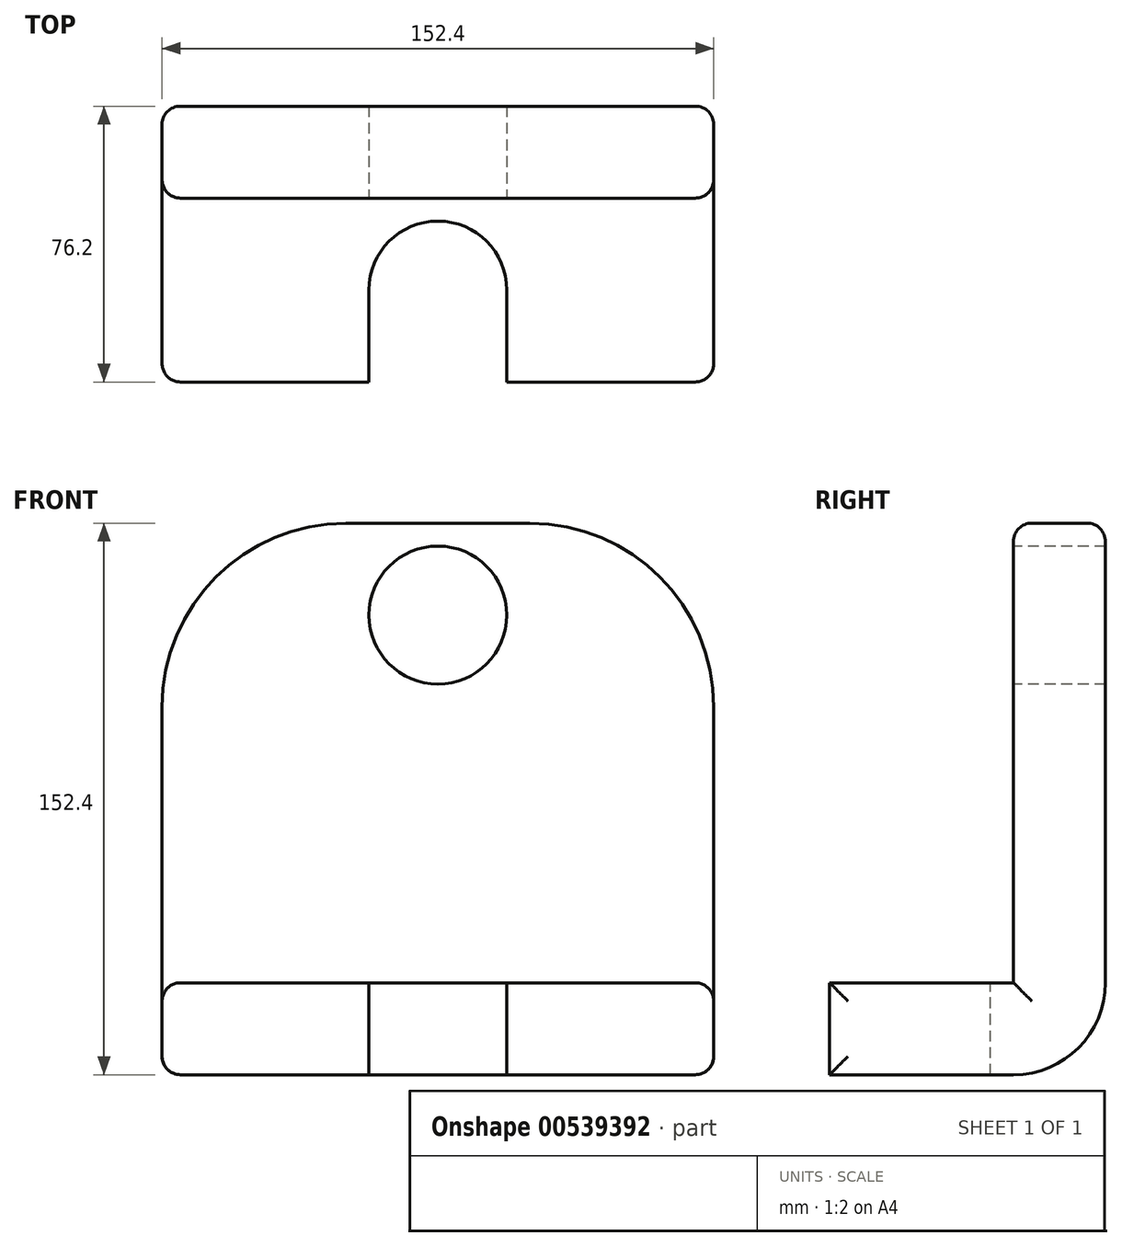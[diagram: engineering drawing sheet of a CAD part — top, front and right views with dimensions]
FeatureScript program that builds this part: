
annotation { "Feature Type Name" : "Feature", "Feature Type Description" : "" }
export const myFeature = defineFeature(function(context is Context, id is Id, definition is map)
    precondition{}
    {
        {
            var Q0;
            Q0=qCreatedBy(makeId("Right.planeOp"),FACE);
            var sketch = newSketch(context, id + "F0", { "sketchPlane" : qUnion([Q0])});
            skLineSegment(sketch, "E0", {"start": v(0, 0) * mm, "end": v(-76.2, 0) * mm});
            skLineSegment(sketch, "E1", {"start": v(-76.2, 0) * mm, "end": v(-76.2, 25.4) * mm});
            skLineSegment(sketch, "E2", {"start": v(-76.2, 25.4) * mm, "end": v(-25.4, 25.4) * mm});
            skLineSegment(sketch, "E3", {"start": v(0, 0) * mm, "end": v(0, 152.4) * mm});
            skLineSegment(sketch, "E4", {"start": v(-25.4, 25.4) * mm, "end": v(-25.4, 152.4) * mm});
            skLineSegment(sketch, "E5", {"start": v(-25.4, 152.4) * mm, "end": v(0, 152.4) * mm});
            skSolve(sketch);
        }
        {
            var Q0;
            Q0=makeQuery(id+"F0.imprint","IMPRINT",FACE,{"disambiguationData":[TD([[makeQuery(id+"F0.imprint","IMPRINT",EDGE,{"derivedFrom":sQuery(id+"F0.wireOp",EDGE,"E0")}),-1.0]])]});
            extrude(context, id + "F1", {"entities" : qUnion([Q0]), "depth" : 76.2 * mm, "offsetDistance" : 25.4 * mm, "hasSecondDirection" : true, "secondDirectionOppositeDirection" : true, "secondDirectionDepth" : 76.2 * mm});
        }
        {
            var Q0;
            Q0=makeQuery(id+"F1.opExtrude","SWEPT_FACE",FACE,{"disambiguationData":[OSD([sQuery(id+"F0.wireOp",EDGE,"E4")])]});
            var sketch = newSketch(context, id + "F2", { "sketchPlane" : qUnion([Q0])});
            skCircle(sketch, "E6", {"center": v(0, 127) * mm, "radius": 19.05 * mm});
            skPoint(sketch, "E6.centerSnap0", {"position": v(0, 152.4) * mm});
            skSolve(sketch);
        }
        {
            var Q0;
            Q0=makeQuery(id+"F2.imprint","IMPRINT",FACE,{"disambiguationData":[TD([[makeQuery(id+"F2.imprint","IMPRINT",EDGE,{"derivedFrom":sQuery(id+"F2.wireOp",EDGE,"E6")}),1.0]])]});
            extrude(context, id + "F3", {"entities" : qUnion([Q0]), "operationType" : NewBodyOperationType.REMOVE, "endBound" : BoundingType.THROUGH_ALL, "oppositeDirection" : true, "depth" : 25.4 * mm, "offsetDistance" : 25.4 * mm});
        }
        {
            var Q0;
            Q0=makeQuery(id+"F1.opExtrude","SWEPT_FACE",FACE,{"disambiguationData":[OSD([sQuery(id+"F0.wireOp",EDGE,"E2")])]});
            var sketch = newSketch(context, id + "F4", { "sketchPlane" : qUnion([Q0])});
            skCircle(sketch, "E7", {"center": v(0, -50.8) * mm, "radius": 19.05 * mm});
            skLineSegment(sketch, "E8", {"start": v(-19.05, -50.8) * mm, "end": v(-19.05, -76.2) * mm});
            skLineSegment(sketch, "E9", {"start": v(19.05, -50.8) * mm, "end": v(19.05, -76.2) * mm});
            skSolve(sketch);
        }
        {
            var Q0;
            {var subQ0=sQuery(id+"F4.wireOp",EDGE,"E8");Q0=makeQuery(id+"F4.imprint","IMPRINT",FACE,{"disambiguationData":[TD([[makeQuery(id+"F4.imprint","IMPRINT",EDGE,{"derivedFrom":subQ0}),1.0]])]});}
            var Q1;
            {var subQ0=sQuery(id+"F4.wireOp",EDGE,"E7");var subQ1=makeQuery(id+"F4.imprint","INTERSECT",VERTEX,{"derivedFrom":[subQ0,sQuery(id+"F4.wireOp",EDGE,"E8")]});Q1=makeQuery(id+"F4.imprint","IMPRINT",FACE,{"disambiguationData":[TD([[makeQuery(id+"F4.imprint","IMPRINT",EDGE,{"disambiguationData":[TD([[subQ1,1.0]])],"derivedFrom":subQ0}),1.0]])]});}
            extrude(context, id + "F5", {"entities" : qUnion([Q0, Q1]), "operationType" : NewBodyOperationType.REMOVE, "endBound" : BoundingType.THROUGH_ALL, "oppositeDirection" : true, "depth" : 25.4 * mm, "offsetDistance" : 25.4 * mm});
        }
        {
            var Q0;
            Q0=makeQuery(id+"F1.opExtrude","CAP_EDGE",EDGE,{"disambiguationData":[OSD([sQuery(id+"F0.wireOp",EDGE,"E5")])],"isStart":false});
            var Q1;
            Q1=makeQuery(id+"F1.opExtrude","CAP_EDGE",EDGE,{"disambiguationData":[OSD([sQuery(id+"F0.wireOp",EDGE,"E5")])],"isStart":true});
            fillet(context, id + "F6", {"entities" : qUnion([Q0, Q1]), "radius" : 50.8 * mm, "tangentPropagation" : true, "allowEdgeOverflow" : false});
        }
        {
            var Q0;
            Q0=makeQuery(id+"F6.opFillet","BLEND_EDGE",EDGE,{"blendedFrom":[makeQuery(id+"F1.opExtrude","CAP_EDGE",EDGE,{"disambiguationData":[OSD([sQuery(id+"F0.wireOp",EDGE,"E5")])],"isStart":false}),makeQuery(id+"F1.opExtrude","SWEPT_FACE",FACE,{"disambiguationData":[OSD([sQuery(id+"F0.wireOp",EDGE,"E4")])]})],"blendedInto":[makeQuery(id+"F1.opExtrude","SWEPT_FACE",FACE,{"disambiguationData":[OSD([sQuery(id+"F0.wireOp",EDGE,"E4")])]})]});
            var Q1;
            Q1=makeQuery(id+"F6.opFillet","BLEND_EDGE",EDGE,{"blendedFrom":[makeQuery(id+"F1.opExtrude","CAP_EDGE",EDGE,{"disambiguationData":[OSD([sQuery(id+"F0.wireOp",EDGE,"E5")])],"isStart":false}),makeQuery(id+"F1.opExtrude","SWEPT_FACE",FACE,{"disambiguationData":[OSD([sQuery(id+"F0.wireOp",EDGE,"E3")])]})],"blendedInto":[makeQuery(id+"F1.opExtrude","SWEPT_FACE",FACE,{"disambiguationData":[OSD([sQuery(id+"F0.wireOp",EDGE,"E3")])]})]});
            var Q2;
            Q2=makeQuery(id+"F1.opExtrude","CAP_EDGE",EDGE,{"disambiguationData":[OSD([sQuery(id+"F0.wireOp",EDGE,"E2")])],"isStart":false});
            var Q3;
            Q3=makeQuery(id+"F1.opExtrude","CAP_FACE",FACE,{"disambiguationData":[OSD([sQuery(id+"F0.wireOp",EDGE,"E0"),sQuery(id+"F0.wireOp",EDGE,"E1"),sQuery(id+"F0.wireOp",EDGE,"E2"),sQuery(id+"F0.wireOp",EDGE,"E3"),sQuery(id+"F0.wireOp",EDGE,"E4"),sQuery(id+"F0.wireOp",EDGE,"E5")])],"isStart":false});
            var Q4;
            Q4=makeQuery(id+"F1.opExtrude","CAP_EDGE",EDGE,{"disambiguationData":[OSD([sQuery(id+"F0.wireOp",EDGE,"E2")])],"isStart":true});
            var Q5;
            Q5=makeQuery(id+"F1.opExtrude","CAP_FACE",FACE,{"disambiguationData":[OSD([sQuery(id+"F0.wireOp",EDGE,"E0"),sQuery(id+"F0.wireOp",EDGE,"E1"),sQuery(id+"F0.wireOp",EDGE,"E2"),sQuery(id+"F0.wireOp",EDGE,"E3"),sQuery(id+"F0.wireOp",EDGE,"E4"),sQuery(id+"F0.wireOp",EDGE,"E5")])],"isStart":true});
            fillet(context, id + "F7", {"entities" : qUnion([Q0, Q1, Q2, Q3, Q4, Q5]), "radius" : 5.08 * mm, "tangentPropagation" : true, "allowEdgeOverflow" : false});
        }
        {
            var Q0;
            Q0=makeQuery(id+"F1.opExtrude","SWEPT_EDGE",EDGE,{"disambiguationData":[OSD([sQuery(id+"F0.wireOp",EDGE,"E0"),sQuery(id+"F0.wireOp",EDGE,"E3")])]});
            fillet(context, id + "F8", {"entities" : qUnion([Q0]), "radius" : 25.4 * mm, "tangentPropagation" : true, "allowEdgeOverflow" : false});
        }
    });
